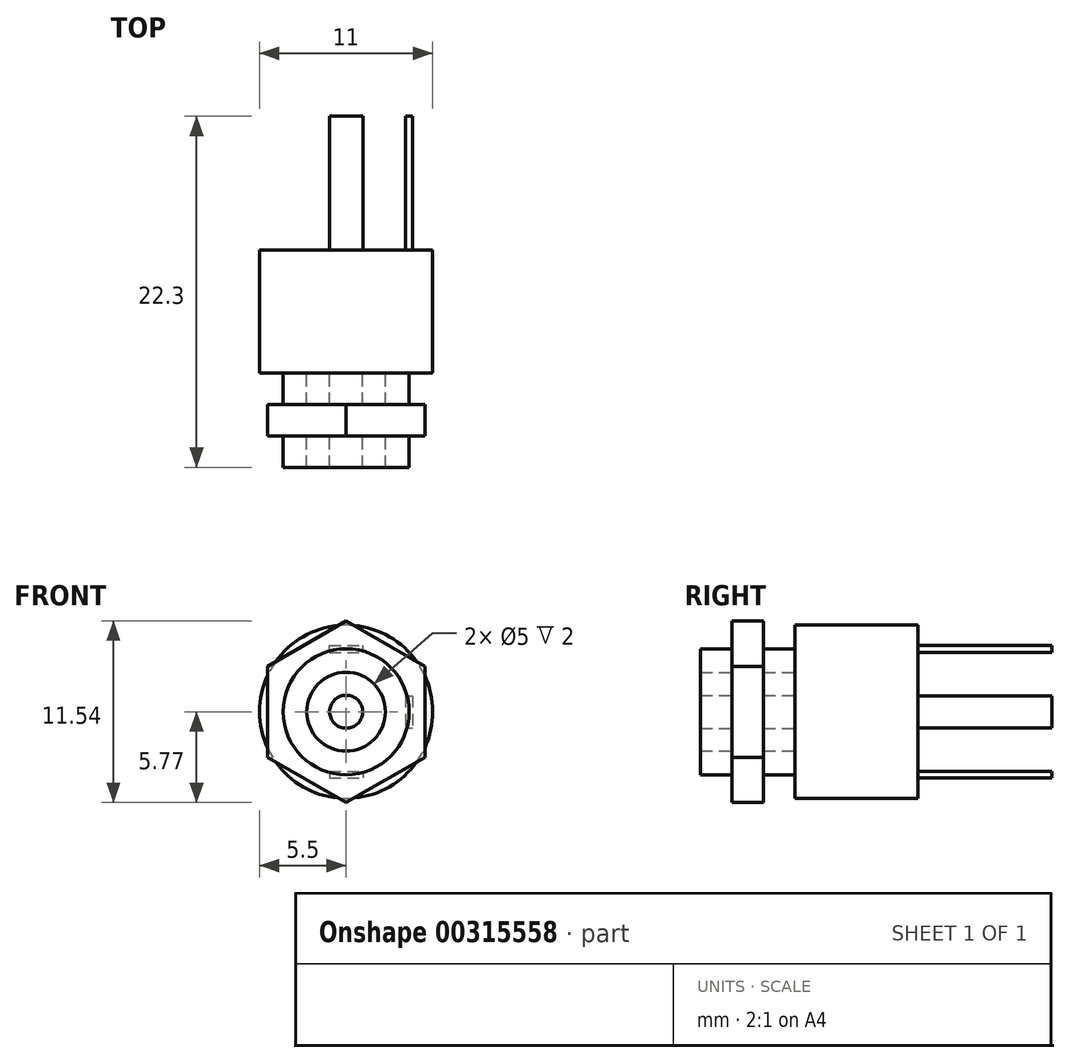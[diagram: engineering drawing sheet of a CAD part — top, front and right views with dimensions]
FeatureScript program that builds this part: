
annotation { "Feature Type Name" : "Feature", "Feature Type Description" : "" }
export const myFeature = defineFeature(function(context is Context, id is Id, definition is map)
    precondition{}
    {
        {
            var Q0;
            Q0=qCreatedBy(makeId("Front.planeOp"),FACE);
            var sketch = newSketch(context, id + "F0", { "sketchPlane" : qUnion([Q0])});
            skCircle(sketch, "E0", {"center": v(0, 0) * mm, "radius": 5.5 * mm});
            skSolve(sketch);
        }
        {
            var Q0;
            Q0 = qSketchRegion(id + "F0", true);
            extrude(context, id + "F1", {"entities" : qUnion([Q0]), "oppositeDirection" : true, "depth" : 7.8 * mm});
        }
        {
            var Q0;
            Q0=qCreatedBy(makeId("Front.planeOp"),FACE);
            var sketch = newSketch(context, id + "F2", { "sketchPlane" : qUnion([Q0])});
            skCircle(sketch, "E1", {"center": v(0, 0) * mm, "radius": 4 * mm});
            skCircle(sketch, "E2", {"center": v(0, 0) * mm, "radius": 2.5 * mm});
            skCircle(sketch, "E3", {"center": v(0, 0) * mm, "radius": 1.05 * mm});
            skSolve(sketch);
        }
        {
            var Q0;
            Q0=makeQuery(id+"F2.imprint","IMPRINT",FACE,{"disambiguationData":[TD([[makeQuery(id+"F2.imprint","IMPRINT",EDGE,{"derivedFrom":sQuery(id+"F2.wireOp",EDGE,"E1")}),1.0]])]});
            var Q1;
            Q1=makeQuery(id+"F2.imprint","IMPRINT",FACE,{"disambiguationData":[TD([[makeQuery(id+"F2.imprint","IMPRINT",EDGE,{"derivedFrom":sQuery(id+"F2.wireOp",EDGE,"E3")}),1.0]])]});
            extrude(context, id + "F3", {"entities" : qUnion([Q0, Q1]), "operationType" : NewBodyOperationType.ADD, "depth" : 6 * mm});
        }
        {
            var Q0;
            Q0=makeQuery(id+"F3.opExtrude","CAP_FACE",FACE,{"disambiguationData":[OSD([sQuery(id+"F2.wireOp",EDGE,"E1"),sQuery(id+"F2.wireOp",EDGE,"E2")])],"isStart":false});
            cPlane(context, id + "F4", {"entities" : qUnion([Q0]), "cplaneType" : CPlaneType.OFFSET, "offset" : 2 * mm, "oppositeDirection" : true, "width" : 150 * mm, "height" : 150 * mm});
        }
        {
            var Q0;
            Q0=qCreatedBy(id+"F4.planeOp",FACE);
            var sketch = newSketch(context, id + "F5", { "sketchPlane" : qUnion([Q0])});
            skCircle(sketch, "E4.cCircle", {"center": v(0, 0) * mm, "radius": 5 * mm, "construction": true});
            skLineSegment(sketch, "E4.0", {"start": v(5, 2.89) * mm, "end": v(5, -2.89) * mm});
            skLineSegment(sketch, "E4.1", {"start": v(5, -2.89) * mm, "end": v(0, -5.77) * mm});
            skLineSegment(sketch, "E4.2", {"start": v(0, -5.77) * mm, "end": v(-5, -2.89) * mm});
            skLineSegment(sketch, "E4.3", {"start": v(-5, -2.89) * mm, "end": v(-5, 2.89) * mm});
            skLineSegment(sketch, "E4.4", {"start": v(-5, 2.89) * mm, "end": v(0, 5.77) * mm});
            skLineSegment(sketch, "E4.5", {"start": v(0, 5.77) * mm, "end": v(5, 2.89) * mm});
            skPoint(sketch, "E4.0.midPoint", {"position": v(5, 0) * mm});
            skSolve(sketch);
        }
        {
            var Q0;
            Q0 = qSketchRegion(id + "F5", true);
            extrude(context, id + "F6", {"entities" : qUnion([Q0]), "operationType" : NewBodyOperationType.ADD, "oppositeDirection" : true, "depth" : 2 * mm});
        }
        {
            var Q0;
            Q0=makeQuery(id+"F1.opExtrude","CAP_FACE",FACE,{"disambiguationData":[OSD([sQuery(id+"F0.wireOp",EDGE,"E0")])],"isStart":false});
            var sketch = newSketch(context, id + "F7", { "sketchPlane" : qUnion([Q0])});
            skLineSegment(sketch, "E5.bottom", {"start": v(4, 4) * mm, "end": v(-4, 4) * mm, "construction": true});
            skLineSegment(sketch, "E5.top", {"start": v(4, -4) * mm, "end": v(-4, -4) * mm, "construction": true});
            skLineSegment(sketch, "E5.left", {"start": v(4, 4) * mm, "end": v(4, -4) * mm, "construction": true});
            skLineSegment(sketch, "E5.right", {"start": v(-4, 4) * mm, "end": v(-4, -4) * mm, "construction": true});
            skPoint(sketch, "E5.middle", {"position": v(0, 0) * mm});
            skLineSegment(sketch, "E6.bottom", {"start": v(-3.77, 1.02) * mm, "end": v(-4.23, 1.02) * mm});
            skLineSegment(sketch, "E6.top", {"start": v(-3.77, -1.02) * mm, "end": v(-4.23, -1.02) * mm});
            skLineSegment(sketch, "E6.left", {"start": v(-3.77, 1.02) * mm, "end": v(-3.77, -1.02) * mm});
            skLineSegment(sketch, "E6.right", {"start": v(-4.23, 1.02) * mm, "end": v(-4.23, -1.02) * mm});
            skPoint(sketch, "E6.middle", {"position": v(-4, 0) * mm});
            skLineSegment(sketch, "E7.bottom", {"start": v(1.07, 3.78) * mm, "end": v(-1.07, 3.78) * mm});
            skLineSegment(sketch, "E7.top", {"start": v(1.07, 4.22) * mm, "end": v(-1.07, 4.22) * mm});
            skLineSegment(sketch, "E7.left", {"start": v(1.07, 3.78) * mm, "end": v(1.07, 4.22) * mm});
            skLineSegment(sketch, "E7.right", {"start": v(-1.07, 3.78) * mm, "end": v(-1.07, 4.22) * mm});
            skPoint(sketch, "E7.middle", {"position": v(0, 4) * mm});
            skLineSegment(sketch, "E8.bottom", {"start": v(1.07, -3.78) * mm, "end": v(-1.07, -3.78) * mm});
            skLineSegment(sketch, "E8.top", {"start": v(1.07, -4.22) * mm, "end": v(-1.07, -4.22) * mm});
            skLineSegment(sketch, "E8.left", {"start": v(1.07, -3.78) * mm, "end": v(1.07, -4.22) * mm});
            skLineSegment(sketch, "E8.right", {"start": v(-1.07, -3.78) * mm, "end": v(-1.07, -4.22) * mm});
            skPoint(sketch, "E8.middle", {"position": v(0, -4) * mm});
            skSolve(sketch);
        }
        {
            var Q0;
            Q0 = qSketchRegion(id + "F7", true);
            extrude(context, id + "F8", {"entities" : qUnion([Q0]), "operationType" : NewBodyOperationType.ADD, "depth" : 8.5 * mm});
        }
    });
